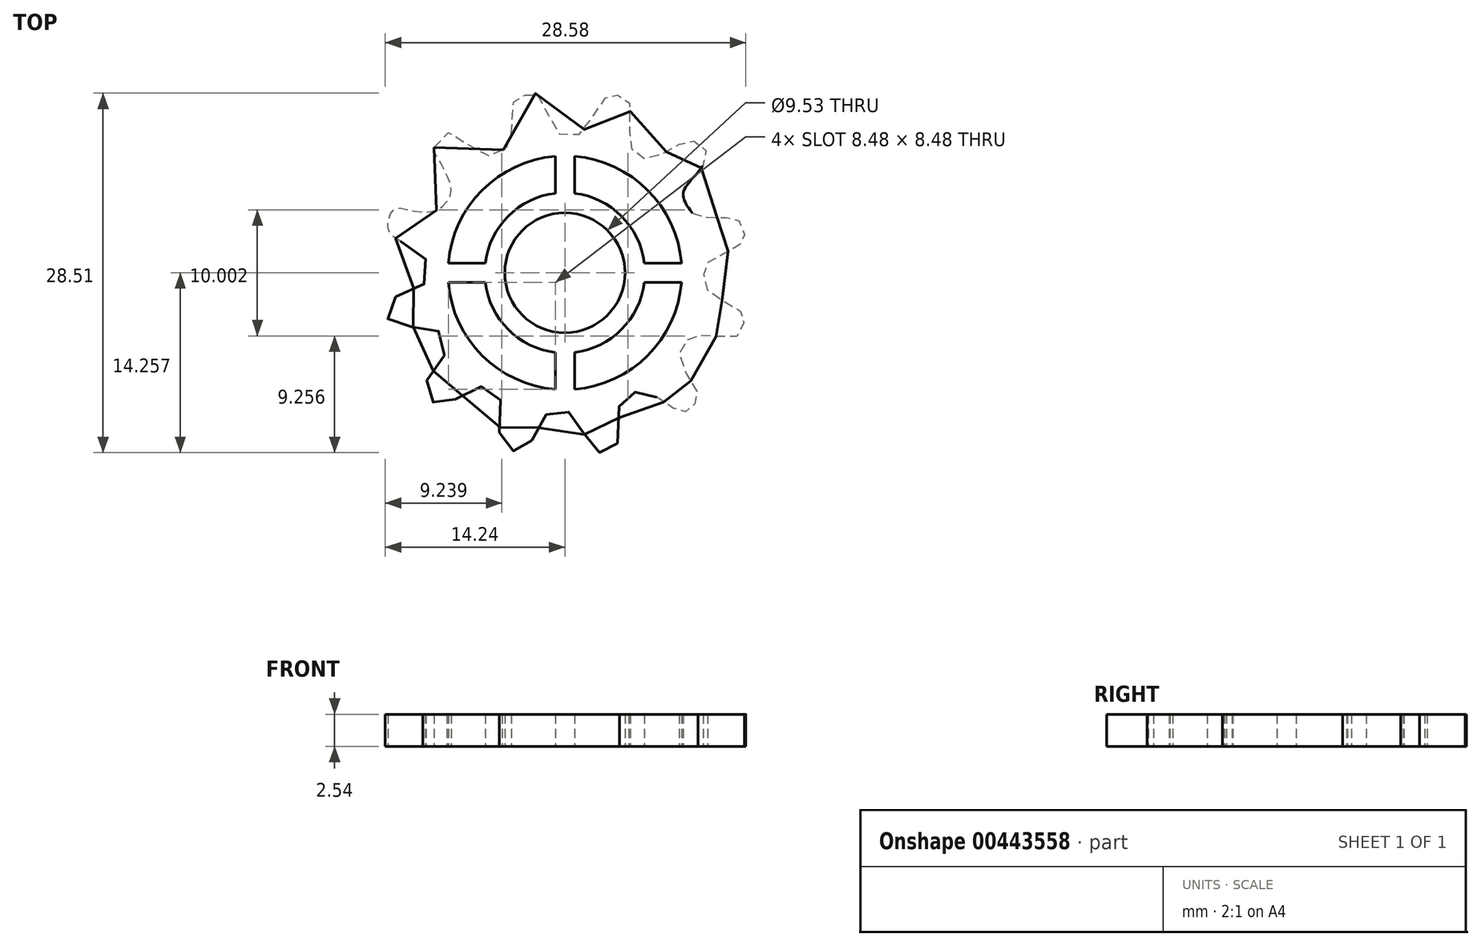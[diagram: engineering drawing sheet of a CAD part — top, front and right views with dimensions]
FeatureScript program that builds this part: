
annotation { "Feature Type Name" : "Feature", "Feature Type Description" : "" }
export const myFeature = defineFeature(function(context is Context, id is Id, definition is map)
    precondition{}
    {
        {
            var Q0;
            Q0=qCreatedBy(makeId("Top.planeOp"),FACE);
            var sketch = newSketch(context, id + "F0", { "sketchPlane" : qUnion([Q0])});
            skPoint(sketch, "E0.middle", {"position": v(0, 0) * mm});
            skPoint(sketch, "E1.start.orphan", {"position": v(-28.3, 14.99) * mm});
            skPoint(sketch, "E2.start.orphan", {"position": v(-22.2, 14.99) * mm});
            skFitSpline(sketch, "E3", {"points": [v(-36.21, 10.7) * mm, v(-35.13, 11.88) * mm, v(-34.6, 11.66) * mm, v(-32.15, 10.14) * mm, v(-31.64, 10.12) * mm, v(-30.24, 10.83) * mm, v(-30.1, 11.54) * mm, v(-29.9, 14.48) * mm, v(-29.76, 14.67) * mm, v(-28.47, 14.99) * mm, v(-28.14, 14.99) * mm, v(-27.7, 14.3) * mm, v(-26.48, 12) * mm, v(-26.2, 11.75) * mm, v(-24.74, 11.75) * mm, v(-24.4, 12.02) * mm, v(-22.9, 14.25) * mm, v(-22.4, 14.86) * mm, v(-21.84, 14.9) * mm, v(-20.92, 14.45) * mm, v(-20.7, 14.14) * mm, v(-20.78, 11.18) * mm, v(-20.65, 10.7) * mm, v(-19.92, 10.1) * mm, v(-19.38, 9.82) * mm, v(-18.13, 10.2) * mm, v(-16.9, 10.89) * mm, v(-16, 11.31) * mm, v(-15.3, 11) * mm, v(-14.66, 10.46) * mm, v(-14.55, 9.93) * mm, v(-15.67, 8.33) * mm, v(-16.47, 7) * mm, v(-15.89, 5.69) * mm, v(-15.27, 5.2) * mm, v(-13.88, 5.2) * mm, v(-12.43, 5.07) * mm, v(-12.08, 4.93) * mm, v(-11.74, 4.1) * mm, v(-11.53, 3.34) * mm, v(-12.15, 2.92) * mm, v(-13.47, 2.16) * mm, v(-14.57, 1.54) * mm, v(-14.78, 1.05) * mm, v(-14.85, 0) * mm, v(-14.23, -0.89) * mm, v(-12.7, -1.79) * mm, v(-11.67, -2.55) * mm, v(-11.67, -3.17) * mm, v(-12.08, -4.2) * mm, v(-12.91, -4.28) * mm, v(-14.64, -4.28) * mm, v(-15.75, -4.2) * mm, v(-16.3, -4.76) * mm, v(-16.79, -5.66) * mm, v(-16.1, -7.46) * mm, v(-15.34, -8.84) * mm, v(-15.44, -9.5) * mm, v(-15.93, -9.92) * mm, v(-16.34, -10.27) * mm, v(-16.83, -10.2) * mm, v(-18.07, -9.44) * mm, v(-19.25, -8.68) * mm, v(-19.87, -8.54) * mm, v(-20.77, -8.95) * mm, v(-21.53, -9.5) * mm, v(-21.53, -10.06) * mm, v(-21.67, -12.55) * mm, v(-21.8, -13.18) * mm, v(-22.64, -13.38) * mm, v(-23.54, -13.45) * mm, v(-24.1, -12.55) * mm, v(-24.92, -10.82) * mm, v(-25.34, -10.34) * mm, v(-26.17, -10.2) * mm, v(-27.07, -10.27) * mm, v(-27.55, -10.82) * mm, v(-28.3, -12.2) * mm, v(-29.08, -13.31) * mm, v(-29.63, -13.45) * mm, v(-30.46, -13.04) * mm, v(-31.01, -12.41) * mm, v(-30.87, -10.9) * mm, v(-30.94, -9.3) * mm, v(-31.44, -8.62) * mm, v(-32.43, -8.26) * mm, v(-33.42, -8.62) * mm, v(-34.85, -9.43) * mm, v(-35.75, -9.78) * mm, v(-36.38, -9.43) * mm, v(-37.1, -8.53) * mm, v(-36.65, -7.54) * mm, v(-35.75, -6.2) * mm, v(-35.2, -5.3) * mm, v(-35.66, -4.13) * mm, v(-36.2, -3.6) * mm, v(-37.45, -3.5) * mm, v(-39.43, -3.5) * mm, v(-39.79, -3.14) * mm, v(-40.06, -1.62) * mm, v(-39.34, -1.17) * mm, v(-37.63, -0.36) * mm, v(-36.92, 0) * mm, v(-36.92, 1.25) * mm, v(-36.92, 1.97) * mm, v(-38.08, 2.87) * mm, v(-39.6, 3.77) * mm, v(-39.88, 4.66) * mm, v(-39.34, 5.83) * mm, v(-38.17, 5.74) * mm, v(-36.29, 5.65) * mm, v(-35.39, 6.19) * mm, v(-34.85, 7.27) * mm, v(-35.2, 8.52) * mm, v(-35.93, 9.87) * mm, v(-36.21, 10.7) * mm]});
            skCircle(sketch, "E4", {"center": v(-25.85, 0.77) * mm, "radius": 4.76 * mm});
            skArc(sketch, "E5", {"start": v(-25.09, 7.07) * mm, "mid": v(-29.77, 5.76) * mm, "end": v(-32.15, 1.53) * mm});
            skArc(sketch, "E6", {"start": v(-26.61, 10) * mm, "mid": v(-32.4, 7.32) * mm, "end": v(-35.1, 1.53) * mm});
            skLineSegment(sketch, "E7.0", {"start": v(-16.61, 1.53) * mm, "end": v(-19.55, 1.53) * mm});
            skLineSegment(sketch, "E8.0", {"start": v(-16.61, 0) * mm, "end": v(-19.55, 0) * mm});
            skLineSegment(sketch, "E9.0", {"start": v(-26.61, 10) * mm, "end": v(-26.61, 7.07) * mm});
            skLineSegment(sketch, "E10.0", {"start": v(-25.09, 10) * mm, "end": v(-25.09, 7.07) * mm});
            skArc(sketch, "E11.trimOffspring", {"start": v(-35.1, 0) * mm, "mid": v(-32.4, -5.79) * mm, "end": v(-26.61, -8.47) * mm});
            skArc(sketch, "E12.trimOffspring", {"start": v(-32.15, 1.53) * mm, "mid": v(-30.34, -3.72) * mm, "end": v(-25.09, -5.54) * mm});
            skLineSegment(sketch, "E13.trimOffspring", {"start": v(-32.15, 1.53) * mm, "end": v(-35.1, 1.53) * mm});
            skLineSegment(sketch, "E14.trimOffspring", {"start": v(-32.15, 0) * mm, "end": v(-35.1, 0) * mm});
            skArc(sketch, "E15.trimOffspring", {"start": v(-25.09, -8.47) * mm, "mid": v(-19.3, -5.79) * mm, "end": v(-16.61, 0) * mm});
            skLineSegment(sketch, "E16.trimOffspring", {"start": v(-26.61, -5.54) * mm, "end": v(-26.61, -8.47) * mm});
            skLineSegment(sketch, "E17.trimOffspring", {"start": v(-25.09, -5.54) * mm, "end": v(-25.09, -8.47) * mm});
            skArc(sketch, "E18.trimOffspring", {"start": v(-25.09, -5.54) * mm, "mid": v(-20.85, -3.15) * mm, "end": v(-19.55, 1.53) * mm});
            skArc(sketch, "E19.trimOffspring", {"start": v(-16.61, 1.53) * mm, "mid": v(-19.3, 7.32) * mm, "end": v(-25.09, 10) * mm});
            skArc(sketch, "E20.trimOffspring", {"start": v(-19.55, 1.53) * mm, "mid": v(-21.36, 5.26) * mm, "end": v(-25.09, 7.07) * mm});
            skCircle(sketch, "E21", {"center": v(-25.85, 0.77) * mm, "radius": 1.65 * mm});
            skSolve(sketch);
        }
        {
            var Q0;
            Q0=makeQuery(id+"F0.imprint","IMPRINT",FACE,{"disambiguationData":[TD([[makeQuery(id+"F0.imprint","IMPRINT",EDGE,{"derivedFrom":sQuery(id+"F0.wireOp",EDGE,"E3")}),-1.0]])]});
            var Q1;
            Q1=makeQuery(id+"F0.imprint","IMPRINT",FACE,{"disambiguationData":[TD([[makeQuery(id+"F0.imprint","IMPRINT",EDGE,{"derivedFrom":sQuery(id+"F0.wireOp",EDGE,"E4")}),-1.0]])]});
            extrude(context, id + "F1", {"entities" : qUnion([Q0, Q1]), "depth" : 2.54 * mm});
        }
    });
